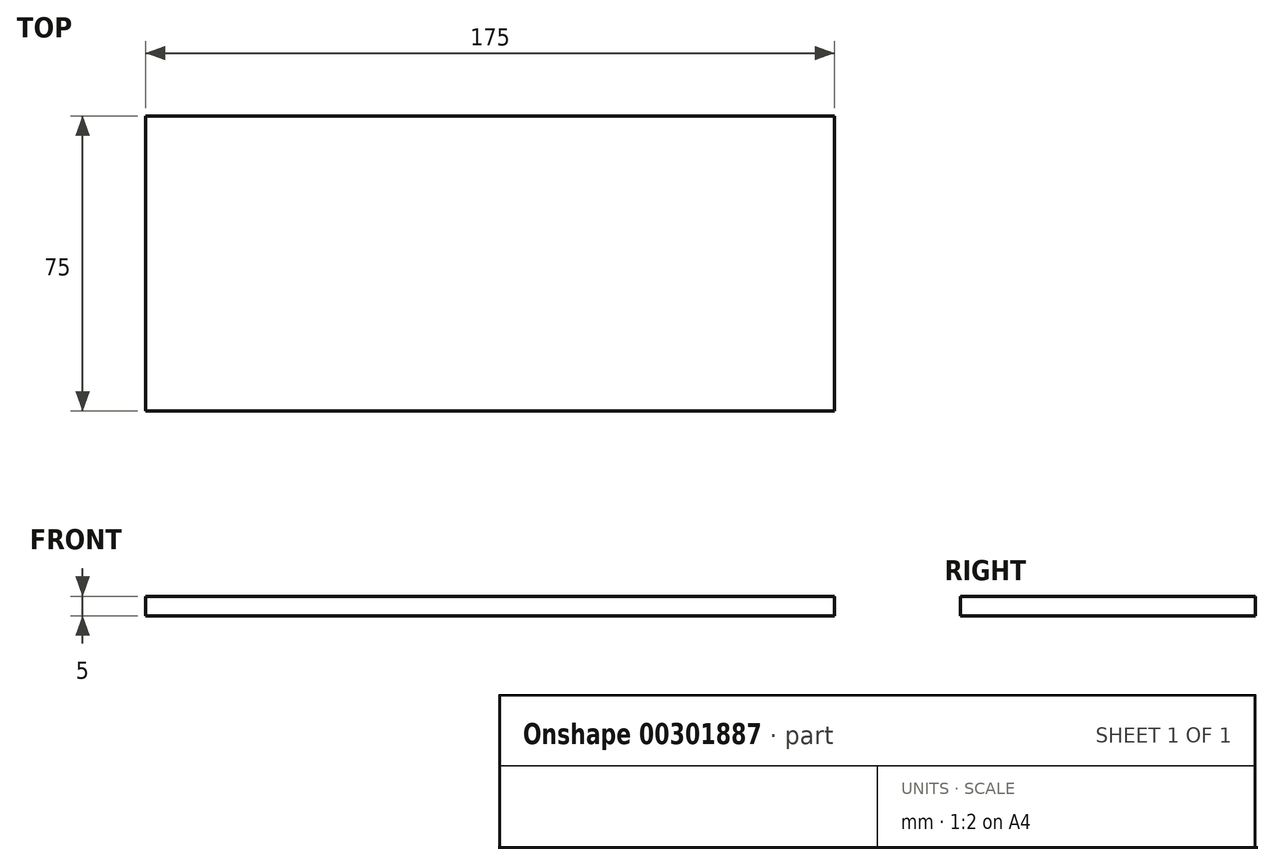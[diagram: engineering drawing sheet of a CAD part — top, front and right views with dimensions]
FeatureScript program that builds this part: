
annotation { "Feature Type Name" : "Feature", "Feature Type Description" : "" }
export const myFeature = defineFeature(function(context is Context, id is Id, definition is map)
    precondition{}
    {
        {
            var Q0;
            Q0=qCreatedBy(makeId("Top.planeOp"),FACE);
            var sketch = newSketch(context, id + "F0", { "sketchPlane" : qUnion([Q0])});
            skLineSegment(sketch, "E0.bottom", {"start": v(0, 0) * mm, "end": v(-175, 0) * mm});
            skLineSegment(sketch, "E0.top", {"start": v(0, 75) * mm, "end": v(-175, 75) * mm});
            skLineSegment(sketch, "E0.left", {"start": v(0, 0) * mm, "end": v(0, 75) * mm});
            skLineSegment(sketch, "E0.right", {"start": v(-175, 0) * mm, "end": v(-175, 75) * mm});
            skSolve(sketch);
        }
        {
            var Q0;
            Q0=makeQuery(id+"F0.imprint","IMPRINT",FACE,{"disambiguationData":[TD([[makeQuery(id+"F0.imprint","IMPRINT",EDGE,{"derivedFrom":sQuery(id+"F0.wireOp",EDGE,"E0.bottom")}),-1.0]])]});
            extrude(context, id + "F1", {"entities" : qUnion([Q0]), "depth" : 5 * mm, "offsetDistance" : 25 * mm});
        }
    });
